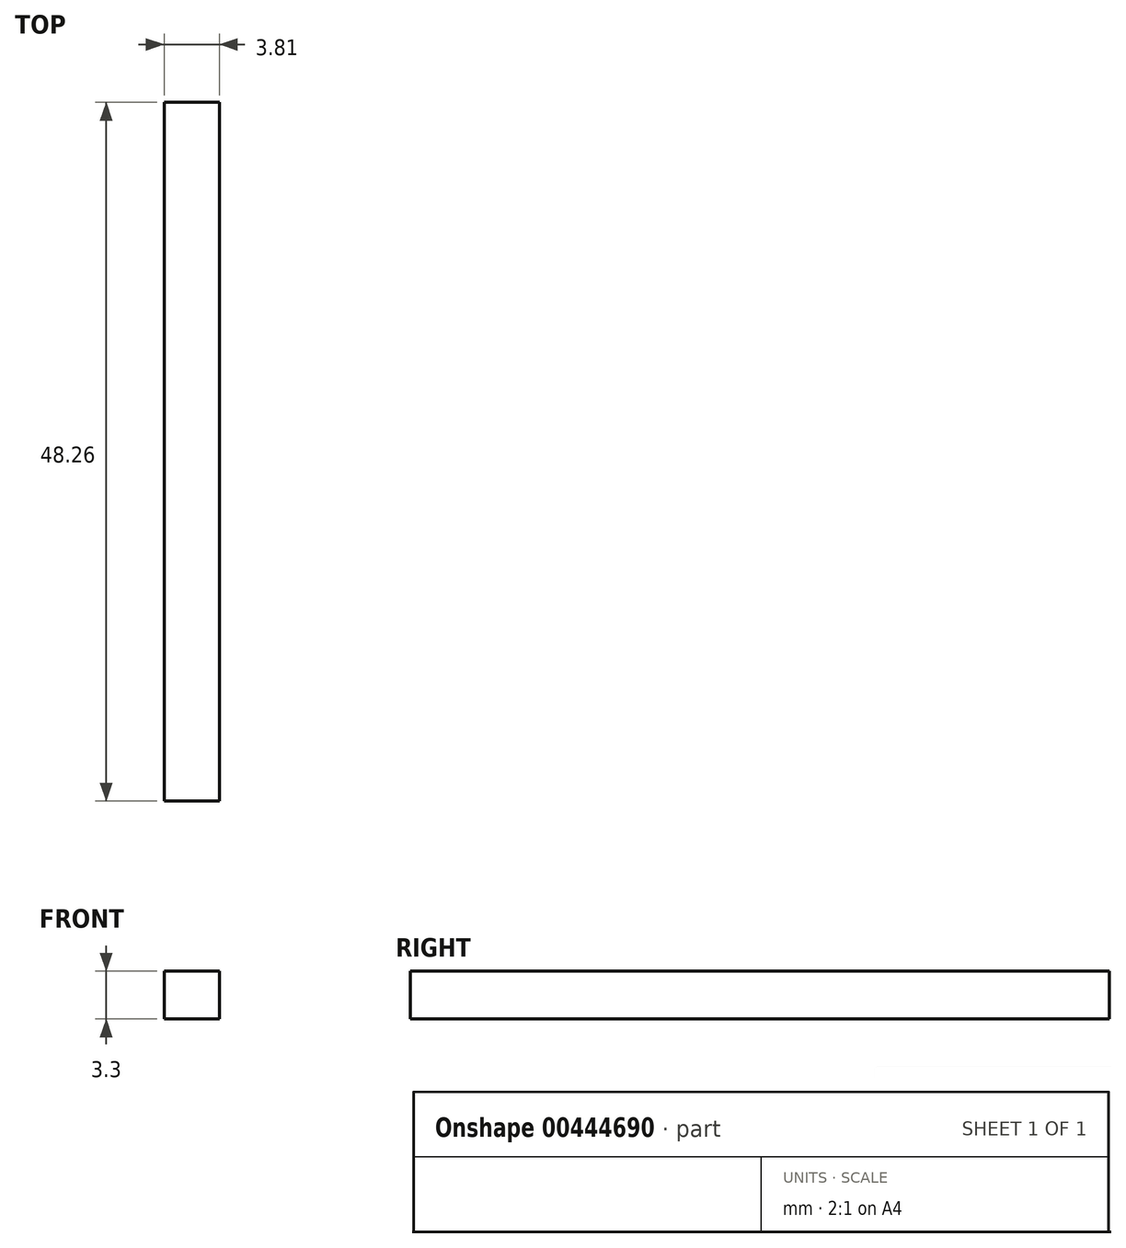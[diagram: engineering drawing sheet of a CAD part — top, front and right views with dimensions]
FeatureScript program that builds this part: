
annotation { "Feature Type Name" : "Feature", "Feature Type Description" : "" }
export const myFeature = defineFeature(function(context is Context, id is Id, definition is map)
    precondition{}
    {
        {
            var Q0;
            Q0=qCreatedBy(makeId("Top.planeOp"),FACE);
            var sketch = newSketch(context, id + "F0", { "sketchPlane" : qUnion([Q0])});
            skLineSegment(sketch, "E0.bottom", {"start": v(-16.28, 49.58) * mm, "end": v(-12.47, 49.58) * mm});
            skLineSegment(sketch, "E0.top", {"start": v(-16.28, 1.32) * mm, "end": v(-12.47, 1.32) * mm});
            skLineSegment(sketch, "E0.left", {"start": v(-16.28, 49.58) * mm, "end": v(-16.28, 1.32) * mm});
            skLineSegment(sketch, "E0.right", {"start": v(-12.47, 49.58) * mm, "end": v(-12.47, 1.32) * mm});
            skSolve(sketch);
        }
        {
            var Q0;
            Q0 = qSketchRegion(id + "F0", true);
            extrude(context, id + "F1", {"entities" : qUnion([Q0]), "depth" : 3.3 * mm});
        }
    });
